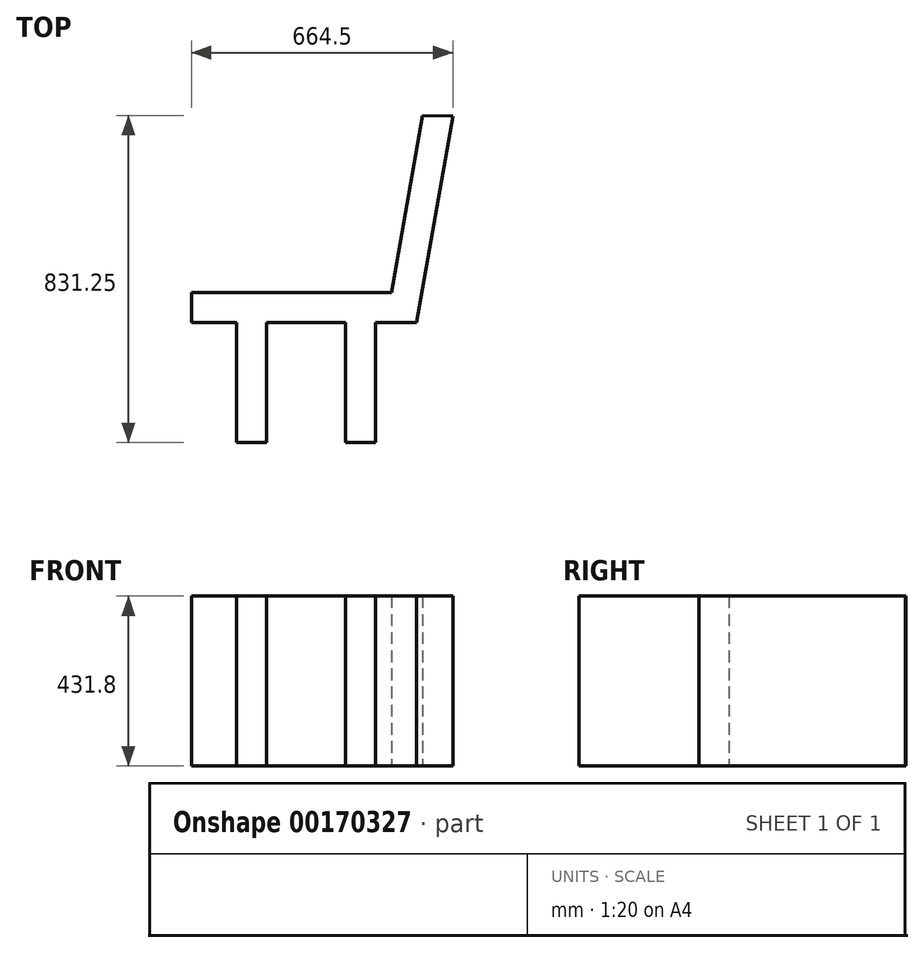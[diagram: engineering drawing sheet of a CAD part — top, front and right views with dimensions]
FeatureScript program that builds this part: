
annotation { "Feature Type Name" : "Feature", "Feature Type Description" : "" }
export const myFeature = defineFeature(function(context is Context, id is Id, definition is map)
    precondition{}
    {
        {
            var Q0;
            Q0=qCreatedBy(makeId("Top.planeOp"),FACE);
            var sketch = newSketch(context, id + "F0", { "sketchPlane" : qUnion([Q0])});
            skPoint(sketch, "E0.middle", {"position": v(0, 0) * mm});
            skLineSegment(sketch, "E1", {"start": v(-269.02, 0) * mm, "end": v(302.92, 0) * mm});
            skLineSegment(sketch, "E2", {"start": v(-269.02, 0) * mm, "end": v(-269.02, 76.2) * mm});
            skLineSegment(sketch, "E3", {"start": v(-269.02, 76.2) * mm, "end": v(238.98, 76.2) * mm});
            skLineSegment(sketch, "E4", {"start": v(302.92, 0) * mm, "end": v(395.48, 524.95) * mm});
            skLineSegment(sketch, "E5", {"start": v(238.98, 76.2) * mm, "end": v(318.37, 526.45) * mm});
            skLineSegment(sketch, "E6", {"start": v(318.37, 526.45) * mm, "end": v(395.48, 524.95) * mm});
            skLineSegment(sketch, "E7", {"start": v(-154.35, 0) * mm, "end": v(-154.35, -304.8) * mm});
            skLineSegment(sketch, "E8", {"start": v(-154.35, -304.8) * mm, "end": v(-78.15, -304.8) * mm});
            skLineSegment(sketch, "E9", {"start": v(-78.15, -304.8) * mm, "end": v(-78.15, 0) * mm});
            skLineSegment(sketch, "E10", {"start": v(122.43, 0) * mm, "end": v(122.43, -304.8) * mm});
            skLineSegment(sketch, "E11", {"start": v(122.43, -304.8) * mm, "end": v(198.63, -304.8) * mm});
            skLineSegment(sketch, "E12", {"start": v(198.63, -304.8) * mm, "end": v(198.63, 0) * mm});
            skSolve(sketch);
        }
        {
            var Q0;
            {var subQ5=sQuery(id+"F0.wireOp",EDGE,"E2");Q0=makeQuery(id+"F0.imprint","IMPRINT",FACE,{"disambiguationData":[TD([[makeQuery(id+"F0.imprint","IMPRINT",EDGE,{"derivedFrom":subQ5}),-1.0]])]});}
            var Q1;
            {var subQ0=sQuery(id+"F0.wireOp",EDGE,"E7");Q1=makeQuery(id+"F0.imprint","IMPRINT",FACE,{"disambiguationData":[TD([[makeQuery(id+"F0.imprint","IMPRINT",EDGE,{"derivedFrom":subQ0}),1.0]])]});}
            var Q2;
            {var subQ0=sQuery(id+"F0.wireOp",EDGE,"E10");Q2=makeQuery(id+"F0.imprint","IMPRINT",FACE,{"disambiguationData":[TD([[makeQuery(id+"F0.imprint","IMPRINT",EDGE,{"derivedFrom":subQ0}),1.0]])]});}
            extrude(context, id + "F1", {"entities" : qUnion([Q0, Q1, Q2]), "depth" : 431.8 * mm});
        }
    });
